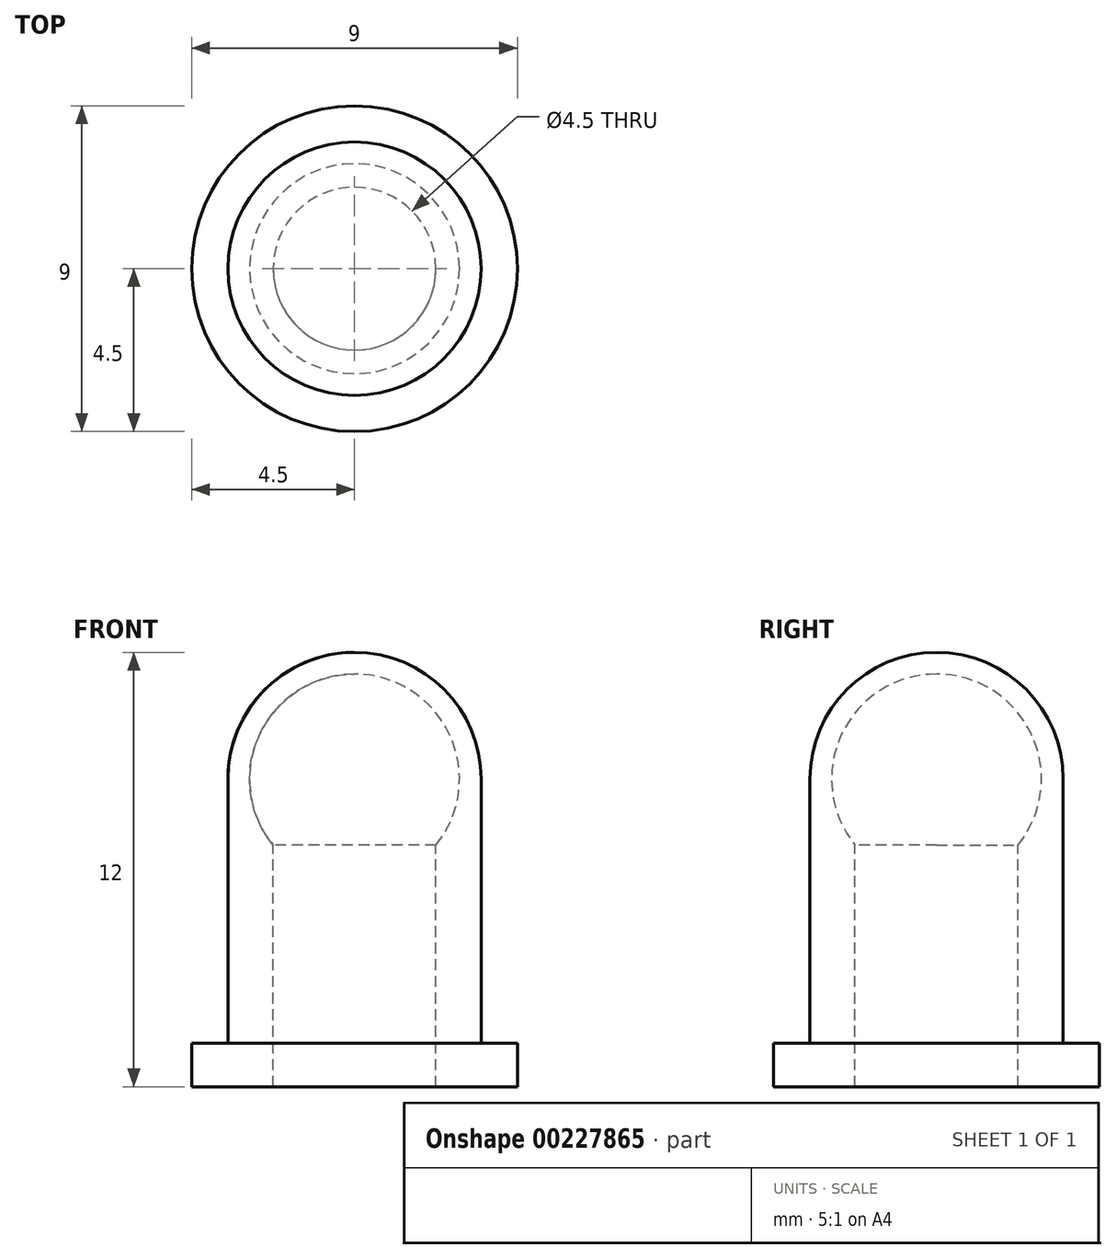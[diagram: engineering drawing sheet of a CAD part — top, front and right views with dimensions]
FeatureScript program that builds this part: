
annotation { "Feature Type Name" : "Feature", "Feature Type Description" : "" }
export const myFeature = defineFeature(function(context is Context, id is Id, definition is map)
    precondition{}
    {
        {
            var Q0;
            Q0=qCreatedBy(makeId("Front.planeOp"),FACE);
            var sketch = newSketch(context, id + "F0", { "sketchPlane" : qUnion([Q0])});
            skLineSegment(sketch, "E0", {"start": v(0, 0) * mm, "end": v(-4.5, 0) * mm, "construction": true});
            skLineSegment(sketch, "E1", {"start": v(-4.5, 0) * mm, "end": v(-4.5, 1.2) * mm});
            skLineSegment(sketch, "E2", {"start": v(-4.5, 1.2) * mm, "end": v(-3.5, 1.2) * mm});
            skLineSegment(sketch, "E3", {"start": v(-3.5, 1.2) * mm, "end": v(-3.5, 8.5) * mm});
            skLineSegment(sketch, "E4", {"start": v(-3.5, 8.5) * mm, "end": v(0, 8.5) * mm, "construction": true});
            skArc(sketch, "E5", {"start": v(-3.5, 8.5) * mm, "mid": v(-2.47, 10.97) * mm, "end": v(0, 12) * mm});
            skLineSegment(sketch, "E6", {"start": v(0, 12) * mm, "end": v(0, 11.4) * mm});
            skLineSegment(sketch, "E7", {"start": v(-4.5, 0) * mm, "end": v(-2.25, 0) * mm});
            skLineSegment(sketch, "E8", {"start": v(-2.25, 0) * mm, "end": v(-2.25, 6.67) * mm});
            skArc(sketch, "E9", {"start": v(0, 11.4) * mm, "mid": v(-2.62, 9.75) * mm, "end": v(-2.25, 6.67) * mm});
            skSolve(sketch);
        }
        {
            var Q0;
            Q0=makeQuery(id+"F0.imprint","IMPRINT",FACE,{"disambiguationData":[TD([[makeQuery(id+"F0.imprint","IMPRINT",EDGE,{"derivedFrom":sQuery(id+"F0.wireOp",EDGE,"E1")}),-1.0]])]});
            var Q1;
            Q1=sQuery(id+"F0.wireOp",EDGE,"E6");
            revolve(context, id + "F1", {"entities" : qUnion([Q0]), "axis" : qUnion([Q1]), "revolveType" : RevolveType.FULL});
        }
    });
